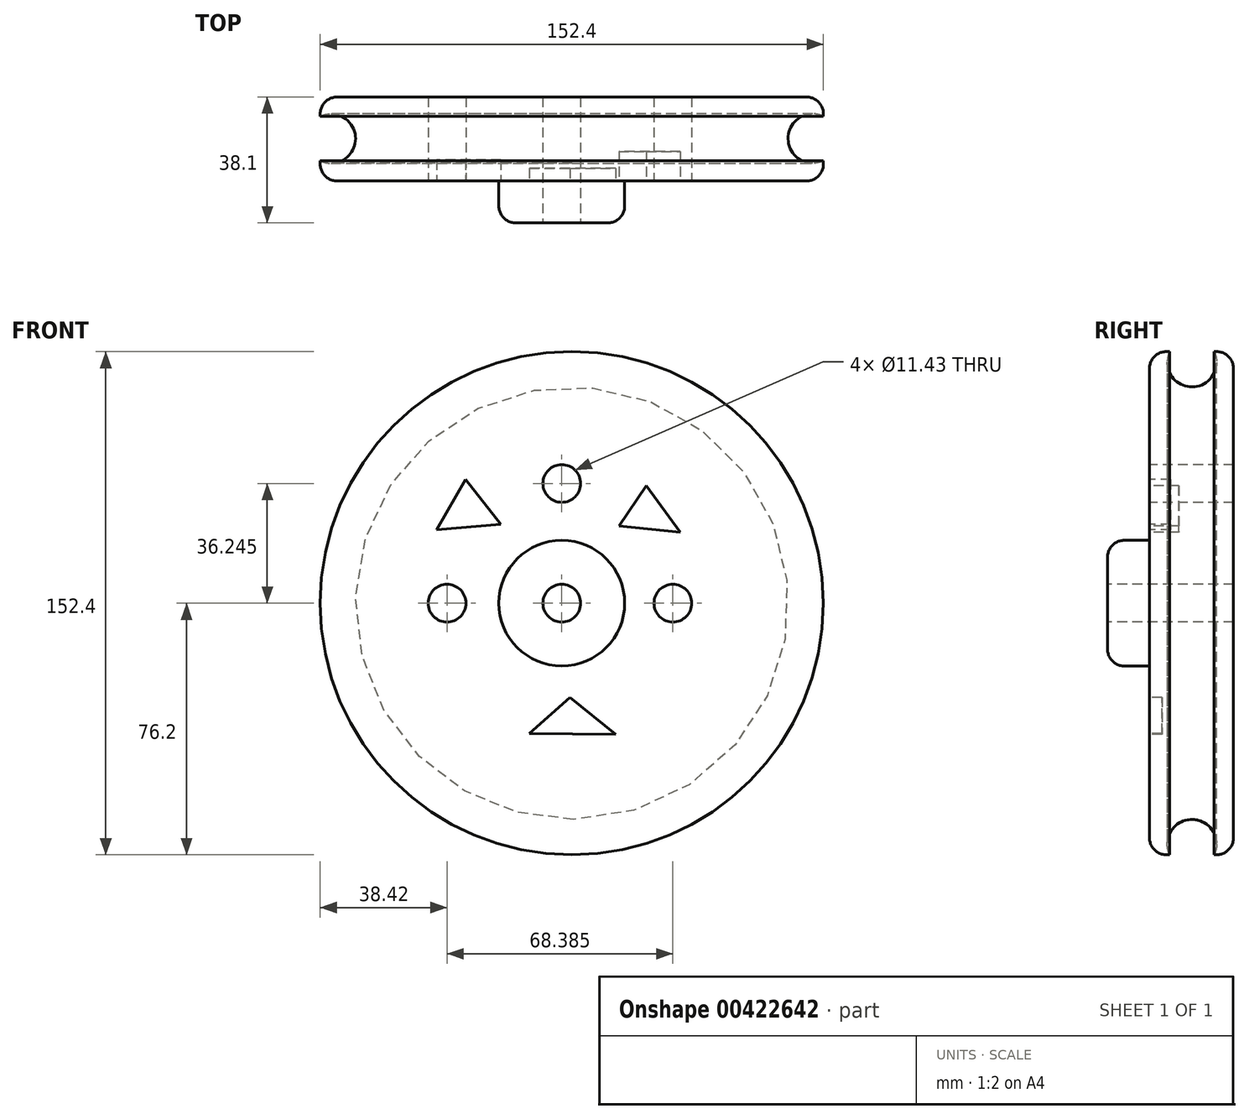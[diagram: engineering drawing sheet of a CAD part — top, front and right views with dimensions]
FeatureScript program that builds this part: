
annotation { "Feature Type Name" : "Feature", "Feature Type Description" : "" }
export const myFeature = defineFeature(function(context is Context, id is Id, definition is map)
    precondition{}
    {
        {
            var Q0;
            Q0=qCreatedBy(makeId("Front.planeOp"),FACE);
            var sketch = newSketch(context, id + "F0", { "sketchPlane" : qUnion([Q0])});
            skCircle(sketch, "E0", {"center": v(3.04, 0) * mm, "radius": 76.2 * mm});
            skSolve(sketch);
        }
        {
            var Q0;
            Q0=makeQuery(id+"F0.imprint","IMPRINT",FACE,{"disambiguationData":[TD([[makeQuery(id+"F0.imprint","IMPRINT",EDGE,{"derivedFrom":sQuery(id+"F0.wireOp",EDGE,"E0")}),1.0]])]});
            extrude(context, id + "F1", {"entities" : qUnion([Q0]), "depth" : 25.4 * mm, "offsetDistance" : 25.4 * mm});
        }
        {
            var Q0;
            Q0=makeQuery(id+"F1.opExtrude","CAP_FACE",FACE,{"disambiguationData":[OSD([sQuery(id+"F0.wireOp",EDGE,"E0")])],"isStart":false});
            var sketch = newSketch(context, id + "F2", { "sketchPlane" : qUnion([Q0])});
            skCircle(sketch, "E1", {"center": v(0, 0) * mm, "radius": 19.05 * mm});
            skPoint(sketch, "E2", {"position": v(5.86, 0) * mm});
            skSolve(sketch);
        }
        {
            var Q0;
            Q0=makeQuery(id+"F2.imprint","IMPRINT",FACE,{"disambiguationData":[TD([[makeQuery(id+"F2.imprint","IMPRINT",EDGE,{"derivedFrom":sQuery(id+"F2.wireOp",EDGE,"E1")}),1.0]])]});
            extrude(context, id + "F3", {"entities" : qUnion([Q0]), "operationType" : NewBodyOperationType.ADD, "depth" : 12.7 * mm, "offsetDistance" : 25.4 * mm});
        }
        {
            var Q0;
            Q0=makeQuery(id+"F1.opExtrude","SWEPT_FACE",FACE,{"disambiguationData":[OSD([sQuery(id+"F0.wireOp",EDGE,"E0")])]});
            fillet(context, id + "F4", {"entities" : qUnion([Q0]), "radius" : 5.08 * mm, "tangentPropagation" : true, "allowEdgeOverflow" : false});
        }
        {
            var Q0;
            Q0=qCreatedBy(makeId("Right.planeOp"),FACE);
            var sketch = newSketch(context, id + "F5", { "sketchPlane" : qUnion([Q0])});
            skCircle(sketch, "E3", {"center": v(-12.57, 72.92) * mm, "radius": 7.48 * mm});
            skPoint(sketch, "E3.first.point", {"position": v(-19.82, 74.76) * mm});
            skPoint(sketch, "E3.second.point", {"position": v(-5.25, 74.47) * mm});
            skPoint(sketch, "E3.third.point", {"position": v(-12.82, 65.44) * mm});
            skSolve(sketch);
        }
        {
            var Q0;
            Q0=makeQuery(id+"F5.imprint","IMPRINT",FACE,{"disambiguationData":[TD([[makeQuery(id+"F5.imprint","IMPRINT",EDGE,{"derivedFrom":sQuery(id+"F5.wireOp",EDGE,"E3")}),1.0]])]});
            var Q1;
            {var subQ0=sQuery(id+"F0.wireOp",EDGE,"E0");Q1=makeQuery(id+"F4.opFillet","BLEND_EDGE",EDGE,{"blendedFrom":[makeQuery(id+"F1.opExtrude","CAP_EDGE",EDGE,{"disambiguationData":[OSD([subQ0])],"isStart":true}),makeQuery(id+"F1.opExtrude","CAP_FACE",FACE,{"disambiguationData":[OSD([subQ0])],"isStart":true})],"blendedInto":[makeQuery(id+"F1.opExtrude","CAP_FACE",FACE,{"disambiguationData":[OSD([subQ0])],"isStart":true})]});}
            revolve(context, id + "F6", {"operationType" : NewBodyOperationType.REMOVE, "entities" : qUnion([Q0]), "axis" : qUnion([Q1]), "revolveType" : RevolveType.FULL, "oppositeDirection" : true});
        }
        {
            var Q0;
            Q0=makeQuery(id+"F2.imprint","IMPRINT",FACE,{"disambiguationData":[TD([[makeQuery(id+"F2.imprint","IMPRINT",EDGE,{"derivedFrom":sQuery(id+"F2.wireOp",EDGE,"E1")}),-1.0]])]});
            var sketch = newSketch(context, id + "F7", { "sketchPlane" : qUnion([Q0])});
            skPoint(sketch, "E4", {"position": v(0, 0) * mm});
            skSolve(sketch);
        }
        {
            var Q0;
            Q0=makeQuery(id+"F3.opExtrude","CAP_FACE",FACE,{"disambiguationData":[OSD([sQuery(id+"F2.wireOp",EDGE,"E1")])],"isStart":false});
            fillet(context, id + "F8", {"entities" : qUnion([Q0]), "radius" : 5.08 * mm, "tangentPropagation" : true, "allowEdgeOverflow" : false});
        }
        {
            var Q0;
            Q0=makeQuery(id+"F3.opExtrude","CAP_FACE",FACE,{"disambiguationData":[OSD([sQuery(id+"F2.wireOp",EDGE,"E1")])],"isStart":false});
            var sketch = newSketch(context, id + "F9", { "sketchPlane" : qUnion([Q0])});
            skCircle(sketch, "E5", {"center": v(0, 0) * mm, "radius": 5.72 * mm});
            skSolve(sketch);
        }
        {
            var Q0;
            Q0 = qSketchRegion(id + "F9", true);
            extrude(context, id + "F10", {"entities" : qUnion([Q0]), "operationType" : NewBodyOperationType.REMOVE, "oppositeDirection" : true, "depth" : 38.1 * mm, "offsetDistance" : 25.4 * mm});
        }
        {
            var Q0;
            Q0=makeQuery(id+"F7.imprint","IMPRINT",FACE,{"disambiguationData":[TD([[makeQuery(id+"F7.imprint","IMPRINT",EDGE,{"derivedFrom":makeQuery(id+"F2.imprint","IMPRINT",EDGE,{"derivedFrom":sQuery(id+"F2.wireOp",EDGE,"E1")})}),-1.0]])]});
            var sketch = newSketch(context, id + "F11", { "sketchPlane" : qUnion([Q0])});
            skCircle(sketch, "E6", {"center": v(0, 36.25) * mm, "radius": 5.72 * mm});
            skSolve(sketch);
        }
        {
            var Q0;
            Q0=sQuery(id+"F11.wireOp",VERTEX,"E6.center");
            var Q1;
            Q1=makeQuery(id+"F1.opExtrude","SWEPT_BODY",BODY,{"disambiguationData":[OSD([sQuery(id+"F0.wireOp",EDGE,"E0")])]});
            hole(context, id + "F12", {"style" : HoleStyle.SIMPLE, "endStyle" : HoleEndStyle.THROUGH, "holeDiameter" : 11.43 * mm, "majorDiameter" : 6.35 * mm, "isTappedThrough" : true, "tappedDepth" : 12.7 * mm, "tapClearance" : 3, "locations" : qUnion([Q0]), "scope" : qUnion([Q1])});
        }
        {
            var Q0;
            Q0=makeQuery(id+"F7.imprint","IMPRINT",FACE,{"disambiguationData":[TD([[makeQuery(id+"F7.imprint","IMPRINT",EDGE,{"derivedFrom":makeQuery(id+"F2.imprint","IMPRINT",EDGE,{"derivedFrom":sQuery(id+"F2.wireOp",EDGE,"E1")})}),-1.0]])]});
            var sketch = newSketch(context, id + "F13", { "sketchPlane" : qUnion([Q0])});
            skCircle(sketch, "E7", {"center": v(-34.74, 0) * mm, "radius": 5.71 * mm});
            skSolve(sketch);
        }
        {
            var Q0;
            Q0=makeQuery(id+"F7.imprint","IMPRINT",FACE,{"disambiguationData":[TD([[makeQuery(id+"F7.imprint","IMPRINT",EDGE,{"derivedFrom":makeQuery(id+"F2.imprint","IMPRINT",EDGE,{"derivedFrom":sQuery(id+"F2.wireOp",EDGE,"E1")})}),-1.0]])]});
            var sketch = newSketch(context, id + "F14", { "sketchPlane" : qUnion([Q0])});
            skCircle(sketch, "E8", {"center": v(33.65, 0) * mm, "radius": 5.71 * mm});
            skSolve(sketch);
        }
        {
            var Q0;
            Q0=sQuery(id+"F13.wireOp",VERTEX,"E7.center");
            var Q1;
            Q1=makeQuery(id+"F1.opExtrude","SWEPT_BODY",BODY,{"disambiguationData":[OSD([sQuery(id+"F0.wireOp",EDGE,"E0")])]});
            hole(context, id + "F15", {"style" : HoleStyle.SIMPLE, "endStyle" : HoleEndStyle.THROUGH, "holeDiameter" : 11.43 * mm, "majorDiameter" : 6.35 * mm, "isTappedThrough" : true, "tappedDepth" : 12.7 * mm, "tapClearance" : 3, "locations" : qUnion([Q0]), "scope" : qUnion([Q1])});
        }
        {
            var Q0;
            Q0=sQuery(id+"F14.wireOp",VERTEX,"E8.center");
            var Q1;
            Q1=makeQuery(id+"F1.opExtrude","SWEPT_BODY",BODY,{"disambiguationData":[OSD([sQuery(id+"F0.wireOp",EDGE,"E0")])]});
            hole(context, id + "F16", {"style" : HoleStyle.SIMPLE, "endStyle" : HoleEndStyle.THROUGH, "holeDiameter" : 11.43 * mm, "majorDiameter" : 6.35 * mm, "isTappedThrough" : true, "tappedDepth" : 12.7 * mm, "tapClearance" : 3, "locations" : qUnion([Q0]), "scope" : qUnion([Q1])});
        }
        {
            var Q0;
            Q0=makeQuery(id+"F7.imprint","IMPRINT",FACE,{"disambiguationData":[TD([[makeQuery(id+"F7.imprint","IMPRINT",EDGE,{"derivedFrom":makeQuery(id+"F2.imprint","IMPRINT",EDGE,{"derivedFrom":sQuery(id+"F2.wireOp",EDGE,"E1")})}),-1.0]])]});
            var sketch = newSketch(context, id + "F17", { "sketchPlane" : qUnion([Q0])});
            skLineSegment(sketch, "E9", {"start": v(-37.94, 22.2) * mm, "end": v(-29.13, 37.44) * mm});
            skLineSegment(sketch, "E10", {"start": v(-29.13, 37.44) * mm, "end": v(-18.42, 23.87) * mm});
            skLineSegment(sketch, "E11", {"start": v(-18.42, 23.87) * mm, "end": v(-37.94, 22.2) * mm});
            skSolve(sketch);
        }
        {
            var Q0;
            Q0 = qSketchRegion(id + "F17", true);
            extrude(context, id + "F18", {"entities" : qUnion([Q0]), "operationType" : NewBodyOperationType.REMOVE, "oppositeDirection" : true, "depth" : 6.35 * mm, "offsetDistance" : 25.4 * mm});
        }
        {
            var Q0;
            Q0=makeQuery(id+"F17.imprint","IMPRINT",FACE,{"disambiguationData":[TD([[makeQuery(id+"F17.imprint","IMPRINT",EDGE,{"derivedFrom":sQuery(id+"F17.wireOp",EDGE,"E9")}),1.0]])]});
            var sketch = newSketch(context, id + "F19", { "sketchPlane" : qUnion([Q0])});
            skLineSegment(sketch, "E12", {"start": v(17.29, 23.4) * mm, "end": v(25.62, 35.54) * mm});
            skLineSegment(sketch, "E13", {"start": v(25.62, 35.54) * mm, "end": v(35.86, 21.5) * mm});
            skLineSegment(sketch, "E14", {"start": v(35.86, 21.5) * mm, "end": v(17.29, 23.4) * mm});
            skSolve(sketch);
        }
        {
            var Q0;
            Q0 = qSketchRegion(id + "F19", true);
            extrude(context, id + "F20", {"entities" : qUnion([Q0]), "operationType" : NewBodyOperationType.REMOVE, "oppositeDirection" : true, "depth" : 8.9 * mm, "offsetDistance" : 25.4 * mm});
        }
        {
            var Q0;
            Q0=makeQuery(id+"F17.imprint","IMPRINT",FACE,{"disambiguationData":[TD([[makeQuery(id+"F17.imprint","IMPRINT",EDGE,{"derivedFrom":sQuery(id+"F17.wireOp",EDGE,"E9")}),1.0]])]});
            var sketch = newSketch(context, id + "F21", { "sketchPlane" : qUnion([Q0])});
            skLineSegment(sketch, "E15", {"start": v(-9.85, -39.45) * mm, "end": v(2.53, -28.5) * mm});
            skLineSegment(sketch, "E16", {"start": v(2.53, -28.5) * mm, "end": v(16.34, -39.68) * mm});
            skLineSegment(sketch, "E17", {"start": v(16.34, -39.68) * mm, "end": v(-9.85, -39.45) * mm});
            skSolve(sketch);
        }
        {
            var Q0;
            Q0 = qSketchRegion(id + "F21", true);
            extrude(context, id + "F22", {"entities" : qUnion([Q0]), "operationType" : NewBodyOperationType.REMOVE, "oppositeDirection" : true, "depth" : 3.8 * mm, "offsetDistance" : 25.4 * mm});
        }
    });
